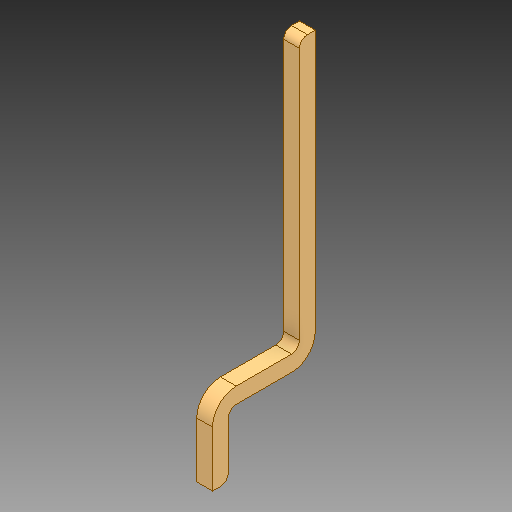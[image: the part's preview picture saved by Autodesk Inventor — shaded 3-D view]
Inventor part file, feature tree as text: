
AUTODESK INVENTOR PART (.ipt)
format: ipt  version: 2018 (Build 220112000, 112)  size: 89,600 bytes
history: native  units: mm
features: fillet x1
ambient origin geometry x8: Origin, YZ Plane, XZ Plane, XY Plane, X Axis, Y Axis, Z Axis, Center Point
bodies: Volumenkörper1 (feature_tree)
feature tree (1):
  fillet  "Fillet1"  [1 undecoded]
note: 1 required parameter value undecoded (feature->parameter linkage not recoverable at this tier; creation-order binding heuristic only, values carry confidence <= 0.55)
